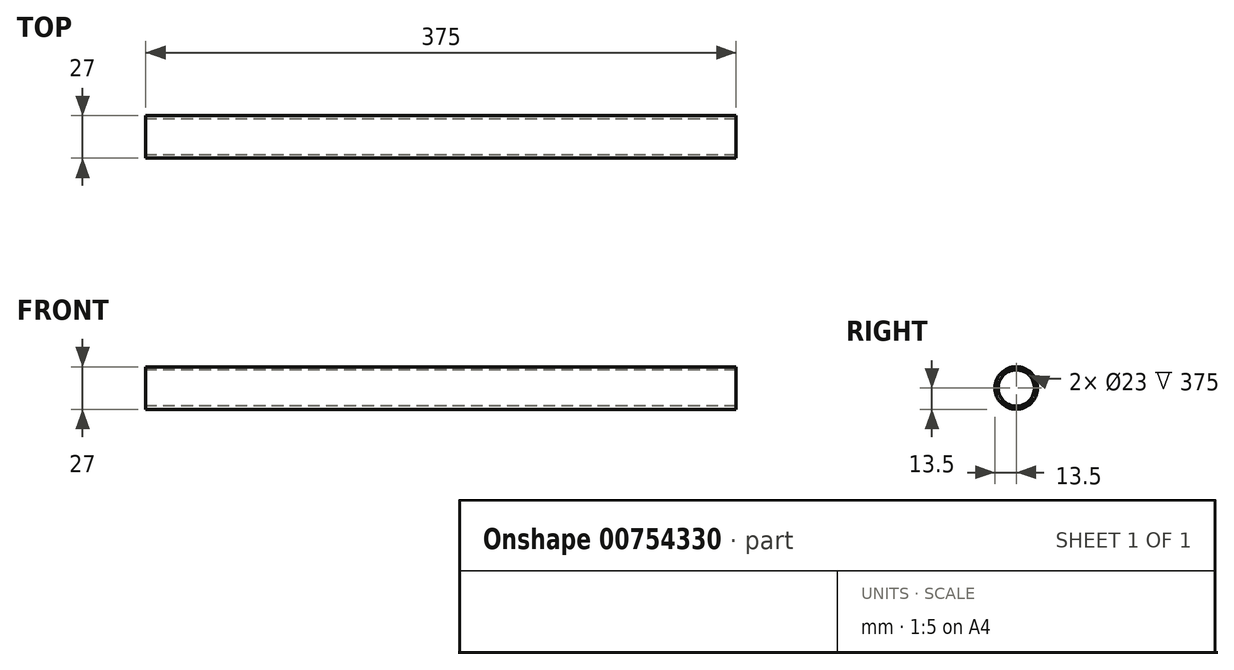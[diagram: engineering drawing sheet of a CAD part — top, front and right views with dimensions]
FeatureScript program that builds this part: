
annotation { "Feature Type Name" : "Feature", "Feature Type Description" : "" }
export const myFeature = defineFeature(function(context is Context, id is Id, definition is map)
    precondition{}
    {
        {
            var Q0;
            Q0=qCreatedBy(makeId("Right.planeOp"),FACE);
            var sketch = newSketch(context, id + "F0", { "sketchPlane" : qUnion([Q0])});
            skCircle(sketch, "E0", {"center": v(0, 0) * mm, "radius": 13.5 * mm});
            skCircle(sketch, "E1", {"center": v(0, 0) * mm, "radius": 11.5 * mm});
            skSolve(sketch);
        }
        {
            var Q0;
            Q0 = qSketchRegion(id + "F0", true);
            extrude(context, id + "F1", {"entities" : qUnion([Q0]), "depth" : 375 * mm, "offsetDistance" : 25 * mm});
        }
    });
